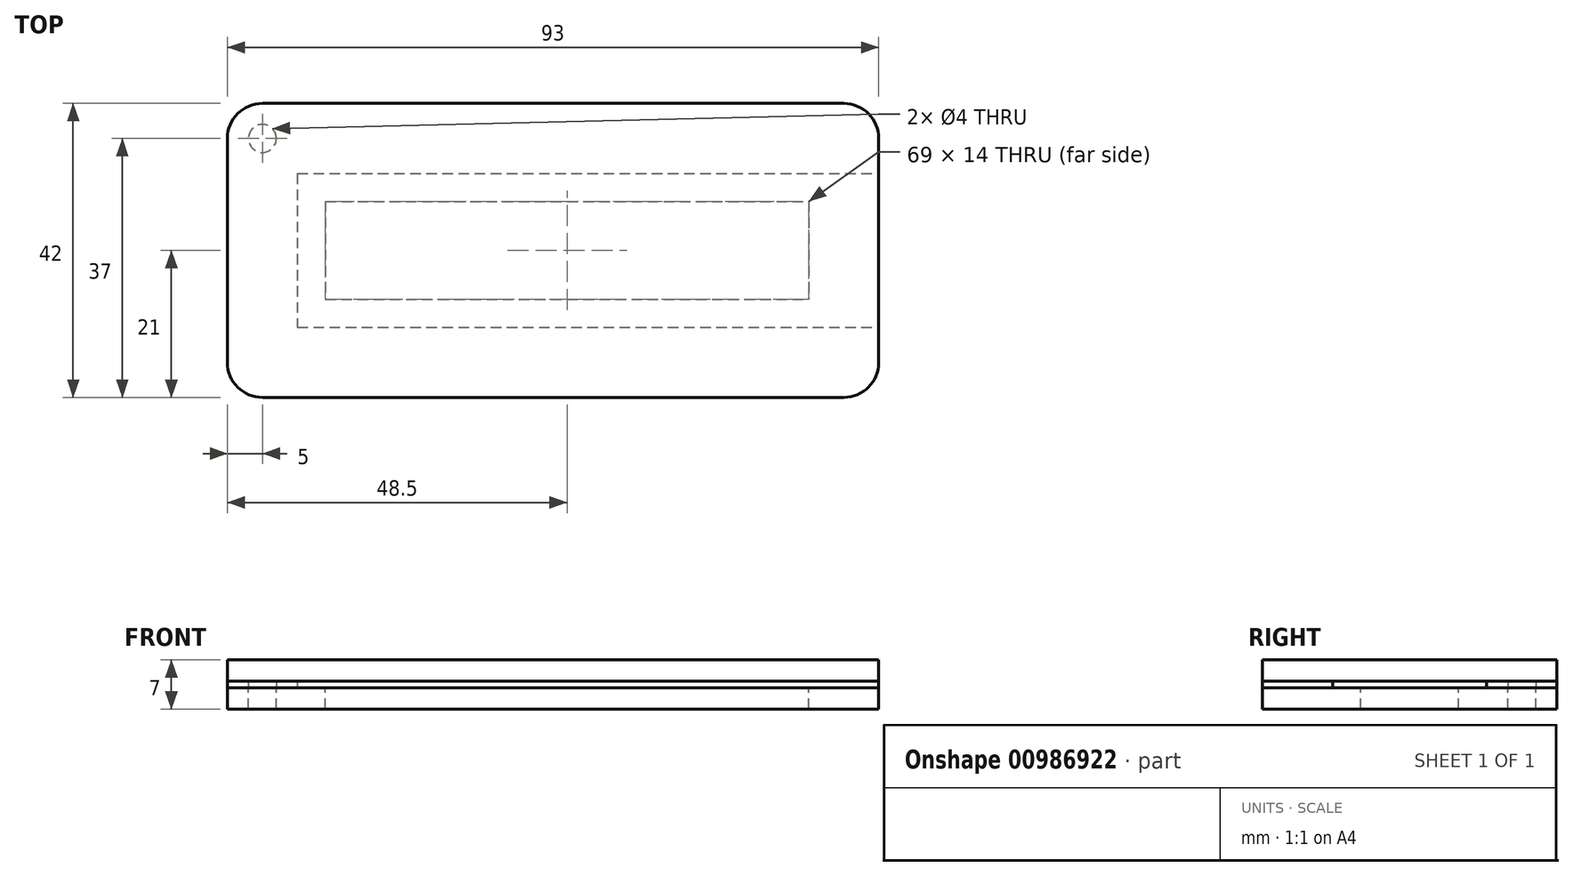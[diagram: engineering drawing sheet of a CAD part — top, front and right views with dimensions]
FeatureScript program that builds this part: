
annotation { "Feature Type Name" : "Feature", "Feature Type Description" : "" }
export const myFeature = defineFeature(function(context is Context, id is Id, definition is map)
    precondition{}
    {
        {
            var Q0;
            Q0=qCreatedBy(makeId("Top.planeOp"),FACE);
            var sketch = newSketch(context, id + "F0", { "sketchPlane" : qUnion([Q0])});
            skLineSegment(sketch, "E0.bottom", {"start": v(-38.5, 11) * mm, "end": v(38.5, 11) * mm, "construction": true});
            skLineSegment(sketch, "E0.top", {"start": v(-38.5, -11) * mm, "end": v(38.5, -11) * mm, "construction": true});
            skLineSegment(sketch, "E0.left", {"start": v(-38.5, 11) * mm, "end": v(-38.5, -11) * mm, "construction": true});
            skLineSegment(sketch, "E0.right", {"start": v(38.5, 11) * mm, "end": v(38.5, -11) * mm, "construction": true});
            skPoint(sketch, "E0.middle", {"position": v(0, 0) * mm});
            skLineSegment(sketch, "E1.bottom", {"start": v(31.5, -3.5) * mm, "end": v(-31.5, -3.5) * mm, "construction": true});
            skLineSegment(sketch, "E1.top", {"start": v(31.5, 3.5) * mm, "end": v(-31.5, 3.5) * mm, "construction": true});
            skLineSegment(sketch, "E1.left", {"start": v(31.5, -3.5) * mm, "end": v(31.5, 3.5) * mm, "construction": true});
            skLineSegment(sketch, "E1.right", {"start": v(-31.5, -3.5) * mm, "end": v(-31.5, 3.5) * mm, "construction": true});
            skLineSegment(sketch, "E2.0", {"start": v(-43.5, 21) * mm, "end": v(39.5, 21) * mm});
            skLineSegment(sketch, "E3.0", {"start": v(-43.5, -21) * mm, "end": v(39.5, -21) * mm});
            skLineSegment(sketch, "E4.0", {"start": v(-48.5, 16) * mm, "end": v(-48.5, -16) * mm});
            skPoint(sketch, "E5.visualSharp", {"position": v(-48.5, 21) * mm});
            skArc(sketch, "E5.filletArc", {"start": v(-43.5, 21) * mm, "mid": v(-47.04, 19.54) * mm, "end": v(-48.5, 16) * mm});
            skArc(sketch, "E6.filletArc", {"start": v(44.5, 16) * mm, "mid": v(43.04, 19.54) * mm, "end": v(39.5, 21) * mm});
            skArc(sketch, "E7.filletArc", {"start": v(39.5, -21) * mm, "mid": v(43.04, -19.54) * mm, "end": v(44.5, -16) * mm});
            skPoint(sketch, "E8.visualSharp", {"position": v(-48.5, -21) * mm});
            skArc(sketch, "E8.filletArc", {"start": v(-48.5, -16) * mm, "mid": v(-47.04, -19.54) * mm, "end": v(-43.5, -21) * mm});
            skLineSegment(sketch, "E9.trimOffspring", {"start": v(44.5, 16) * mm, "end": v(44.5, -16) * mm});
            skCircle(sketch, "E10", {"center": v(-43.5, 16) * mm, "radius": 2 * mm});
            skLineSegment(sketch, "E11.0", {"start": v(-34.5, 7) * mm, "end": v(34.5, 7) * mm});
            skLineSegment(sketch, "E12.0", {"start": v(-34.5, 7) * mm, "end": v(-34.5, -7) * mm});
            skLineSegment(sketch, "E13.0", {"start": v(-34.5, -7) * mm, "end": v(34.5, -7) * mm});
            skLineSegment(sketch, "E14.0", {"start": v(34.5, 7) * mm, "end": v(34.5, -7) * mm});
            skSolve(sketch);
        }
        {
            var Q0;
            Q0=makeQuery(id+"F0.imprint","IMPRINT",FACE,{"disambiguationData":[TD([[makeQuery(id+"F0.imprint","IMPRINT",EDGE,{"derivedFrom":sQuery(id+"F0.wireOp",EDGE,"E2.0")}),-1.0]])]});
            extrude(context, id + "F1", {"entities" : qUnion([Q0]), "oppositeDirection" : true, "depth" : 3 * mm, "offsetDistance" : 25 * mm});
        }
        {
            var Q0;
            Q0=makeQuery(id+"F1.opExtrude","CAP_FACE",FACE,{"disambiguationData":[OSD([sQuery(id+"F0.wireOp",EDGE,"E2.0"),sQuery(id+"F0.wireOp",EDGE,"6078586f-2925-421f-b626-a31353567f25.0"),sQuery(id+"F0.wireOp",EDGE,"E3.0"),sQuery(id+"F0.wireOp",EDGE,"E4.0"),sQuery(id+"F0.wireOp",EDGE,"E5.filletArc"),sQuery(id+"F0.wireOp",EDGE,"E6.filletArc"),sQuery(id+"F0.wireOp",EDGE,"E7.filletArc"),sQuery(id+"F0.wireOp",EDGE,"E8.filletArc"),sQuery(id+"F0.wireOp",EDGE,"JzD72Hnu-pBGd-Yzs9-XRAp-TnaH23AVerOi"),sQuery(id+"F0.wireOp",EDGE,"E9.trimOffspring"),sQuery(id+"F0.wireOp",EDGE,"ee2381e4-39eb-49d0-ad47-ff90151cd445.filletArc"),sQuery(id+"F0.wireOp",EDGE,"b74bfb7d-baeb-4252-b897-a5c72af31514.filletArc"),sQuery(id+"F0.wireOp",EDGE,"E10"),sQuery(id+"F0.wireOp",EDGE,"E11.0"),sQuery(id+"F0.wireOp",EDGE,"E12.0"),sQuery(id+"F0.wireOp",EDGE,"E13.0"),sQuery(id+"F0.wireOp",EDGE,"E14.0"),sQuery(id+"F0.wireOp",EDGE,"f92646e1-c5d6-444b-9126-484f78f2b60e.trimOffspring")])],"isStart":true});
            var sketch = newSketch(context, id + "F2", { "sketchPlane" : qUnion([Q0])});
            skLineSegment(sketch, "E15.0.8", {"start": v(44.5, 11) * mm, "end": v(44.5, 16) * mm});
            skArc(sketch, "E15.0.9", {"start": v(44.5, 16) * mm, "mid": v(43.04, 19.54) * mm, "end": v(39.5, 21) * mm});
            skLineSegment(sketch, "E15.0.10", {"start": v(39.5, 21) * mm, "end": v(-43.5, 21) * mm});
            skArc(sketch, "E15.0.11", {"start": v(-43.5, 21) * mm, "mid": v(-47.04, 19.54) * mm, "end": v(-48.5, 16) * mm});
            skLineSegment(sketch, "E15.0.12", {"start": v(-48.5, 16) * mm, "end": v(-48.5, -16) * mm});
            skArc(sketch, "E15.0.13", {"start": v(-48.5, -16) * mm, "mid": v(-47.04, -19.54) * mm, "end": v(-43.5, -21) * mm});
            skLineSegment(sketch, "E15.0.14", {"start": v(-43.5, -21) * mm, "end": v(39.5, -21) * mm});
            skArc(sketch, "E15.0.15", {"start": v(39.5, -21) * mm, "mid": v(43.04, -19.54) * mm, "end": v(44.5, -16) * mm});
            skLineSegment(sketch, "E15.0.16", {"start": v(44.5, -16) * mm, "end": v(44.5, -11) * mm});
            skCircle(sketch, "E16.0", {"center": v(-43.5, 16) * mm, "radius": 2 * mm});
            skPoint(sketch, "E17.0", {"position": v(-38.5, 11) * mm});
            skLineSegment(sketch, "E18.bottom", {"start": v(-38.5, 11) * mm, "end": v(44.5, 11) * mm});
            skLineSegment(sketch, "E18.top", {"start": v(-38.5, -11) * mm, "end": v(44.5, -11) * mm});
            skLineSegment(sketch, "E18.left", {"start": v(-38.5, 11) * mm, "end": v(-38.5, -11) * mm});
            skPoint(sketch, "E19.0", {"position": v(38.5, -11) * mm});
            skLineSegment(sketch, "E20.0", {"start": v(44.5, 16) * mm, "end": v(44.5, -16) * mm, "construction": true});
            skSolve(sketch);
        }
        {
            var Q0;
            Q0 = qSketchRegion(id + "F2", true);
            extrude(context, id + "F3", {"entities" : qUnion([Q0]), "depth" : 1 * mm, "offsetDistance" : 25 * mm});
        }
        {
            var Q0;
            Q0=makeQuery(id+"F3.opExtrude","CAP_FACE",FACE,{"disambiguationData":[OSD([sQuery(id+"F2.wireOp",EDGE,"E15.0.8"),sQuery(id+"F2.wireOp",EDGE,"E15.0.9"),sQuery(id+"F2.wireOp",EDGE,"E15.0.10"),sQuery(id+"F2.wireOp",EDGE,"E15.0.11"),sQuery(id+"F2.wireOp",EDGE,"E15.0.12"),sQuery(id+"F2.wireOp",EDGE,"E15.0.13"),sQuery(id+"F2.wireOp",EDGE,"E15.0.14"),sQuery(id+"F2.wireOp",EDGE,"E15.0.15"),sQuery(id+"F2.wireOp",EDGE,"E15.0.16"),sQuery(id+"F2.wireOp",EDGE,"E16.0"),sQuery(id+"F2.wireOp",EDGE,"E18.bottom"),sQuery(id+"F2.wireOp",EDGE,"E18.top"),sQuery(id+"F2.wireOp",EDGE,"E18.left")])],"isStart":false});
            var sketch = newSketch(context, id + "F4", { "sketchPlane" : qUnion([Q0])});
            skArc(sketch, "E21.0.4", {"start": v(44.5, 16) * mm, "mid": v(43.04, 19.54) * mm, "end": v(39.5, 21) * mm});
            skLineSegment(sketch, "E21.0.5", {"start": v(39.5, 21) * mm, "end": v(-43.5, 21) * mm});
            skArc(sketch, "E21.0.6", {"start": v(-43.5, 21) * mm, "mid": v(-47.04, 19.54) * mm, "end": v(-48.5, 16) * mm});
            skLineSegment(sketch, "E21.0.7", {"start": v(-48.5, 16) * mm, "end": v(-48.5, -16) * mm});
            skArc(sketch, "E21.0.8", {"start": v(-48.5, -16) * mm, "mid": v(-47.04, -19.54) * mm, "end": v(-43.5, -21) * mm});
            skLineSegment(sketch, "E21.0.9", {"start": v(-43.5, -21) * mm, "end": v(39.5, -21) * mm});
            skArc(sketch, "E21.0.10", {"start": v(39.5, -21) * mm, "mid": v(43.04, -19.54) * mm, "end": v(44.5, -16) * mm});
            skLineSegment(sketch, "E22", {"start": v(44.5, 16) * mm, "end": v(44.5, -16) * mm});
            skSolve(sketch);
        }
        {
            var Q0;
            Q0 = qSketchRegion(id + "F4", true);
            extrude(context, id + "F5", {"entities" : qUnion([Q0]), "depth" : 3 * mm, "offsetDistance" : 25 * mm});
        }
    });
